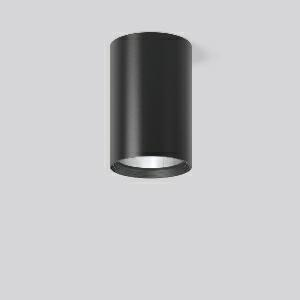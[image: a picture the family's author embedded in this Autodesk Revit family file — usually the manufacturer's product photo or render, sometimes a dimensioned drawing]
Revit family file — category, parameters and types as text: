
# Revit family: heledon_maxi_a_931219_003_2_76_6cf1
name_source: partatom
category: Lighting Fixtures
units: mm (PartAtom-declared; Revit-internal decimal feet)

## family parameters
Cut with Voids When Loaded = No
Host = Face
Light Source = No
Part Type = Normal
Room Calculation Point = No
Round Connector Dimension = Use Diameter
Shared = No

## types (1)
- HELEDON maxi A (1 x LED Modul 927, 3050 lm, 2700)
    Apparent Load = 25 VA
    Approval mark = CE
    CIE Flux Codes = 97 100 100 100 100
    Color Rendering = 92
    Color Temperature = 2700
    Default Elevation = 1800 mm
    Description = Series: HELEDON maxi
Cylindrical surface-mounted downlight. Housing: die-cast aluminium, powder-coated. Internal ceiling frame polycarbonate with bayonet mounting. Black plastic ring and recessed LED to prevent glare from the side. Optical assembly with reflector made of MIRO-Silver with 98% total light reflection for outstanding efficiency - can be changed without tools. Best colour rendering index Ra>90. Suitable for Ceiling mounting. Easy installation with a separate ceiling frame with bayonet mounting and plug connection. Driver integrated. Connected via plug-in connector. High quality converter without flickering and stroboscopic effect. The following accessories can be mounted without use of tools: interchangeable lenses, decorative glasses, honeycomb louvre, clear and frosted diffusers, white interchangeable plastic ring. 
Colour: deep black, matt (RAL 9005)
Diameter: 123 mm
Height: 183 mm
Lamp: LED
Socket: without socket
Colour temperature: 2700K
Colour rendering index (CRI): 92
System power: 25 W
Rated luminous flux: 3050 lm
Luminous efficiency: 122 lm/W
Control gear: Converter, dimmable, DALI
Protection class: I
Type of protection: IP 20
    Height = 183 mm
    Lamp = 1 x LED Modul 927
    Lamp Light Flux = 3050 lm
    Lamp count = 1
    Length = 123 mm
    Lifetime = 50000 h
    Luminous efficacy = 122 lm/W
    Manufacturer = RZB
    ModVariant = No
    Model = 931219.003.2.76
    Mounting Place = Ceiling
    Mounting Type = Surface mounted
    Number of Poles = 1
    OnlyDefault = Yes
    Power Factor = 1
    Product Name = HELEDON maxi A
    Product group = Surface mounted downlights
    ProductGroupID = 302
    Protection Class = Protection class I
    Protection Degree = IP 20
    RLX_Detail_Level = 1
    RLX_Emergency_Light_Flux = 0 lm
    RLX_Emergency_Type = 0
    RLX_Emergency_Type_DB = No
    RlxData = <blob elided: 95757 chars, md5=a5252de9>
    Socket = socket
    Standby Power = 0 W
    System Light Flux = 3050 lm
    System Power = 25 W
    Type Comments = Product without accessories
    Type Image = 931192.003.jpg
    URL = http://relux.com
    VarID = ---
    Voltage = 230 V
    Voltage Range = 220-240 V
    Weight = 0.00 kg
    Width = 0 mm  [stored 0 ft]

note: [stored X ft] marks values corroborated as IEEE doubles in the binary element streams (Revit-internal decimal feet)

## geometry (parser evidence)
native form markers: Blend x4, Sweep x10
no freeform markers — native parametric forms only
